# Revit family: LIXIL - CC-CISTERN N - COBRA CISTERN CONCEALED
name_source: partatom
category: Plumbing Fixtures
units: mm (PartAtom-declared; Revit-internal decimal feet)

## family parameters
Always vertical = Yes
Cut with Voids When Loaded = No
Enable Cutting in Views = No
Maintain Annotation Orientation = No
OmniClass Number = 23.45.00.00
OmniClass Title = Sanitary, Laundry, and Cleaning Equipment
Part Type = Normal
Room Calculation Point = No
Round Connector Dimension = Use Diameter
Shared = Yes
Work Plane-Based = No

## types (1)
- CC-CISTERN N
    Default Elevation = 0 mm  [stored 0 ft]
    Description = Cobra Cistern Concealed to detail and spec. See sanware schedule. Available from Lixil.
    HEIGHT = 285 mm  [stored 0.935039 ft]
    Hosted on lixil.co.za = https://www.lixil.co.za
    M _ CISTERN _ BODY = M _ LIXIL - PLASTIC - WHITE 02
    M _ CISTERN _ BODY 02 = M _ LIXIL - PLASTIC - WHITE 01
    M _ CISTERN _ BRASS = M _ LIXIL - BRASS 01
    M _ CISTERN _ FIXING 01 = M _ LIXIL - PLASTIC - GREY 01
    M _ CISTERN _ PIPE 01 = M _ LIXIL - PLASTIC - WHITE 02
    M _ RUBBER _ WHITE _ SOFT = M _ LIXIL - RUBBER - WHITE 01
    Product Specification = Supplier: Lixil.
Product description: DIY friendly concealed cistern, with compression resistant reinforced tank. Mechanical actuation mechanism. Easy access click fit components for simplified maintenance.
Product Code: CENSHJNN-2CO
SKU Code: CC-CISTERN/N
Barcode: 6002194051381
Brand: Cobra
Range: Cobra
Category: Flush Valves
Sub-Category: Toilets
Package Height: 130 mm
Package Width: 500 mm
Package Length: 760 mm
Package Volume: 49400000 mm³
Package Weight: 3.96 kg

Notes:
- Refer to manufacturer's and supplier's installation, maintenance and cleaning manual.
- Refer to manufacturer's and supplier's guarantees and warrantees document.

note: [stored X ft] marks values corroborated as IEEE doubles in the binary element streams (Revit-internal decimal feet)

## geometry (parser evidence)
native form markers: Sweep x16
no freeform markers — native parametric forms only
